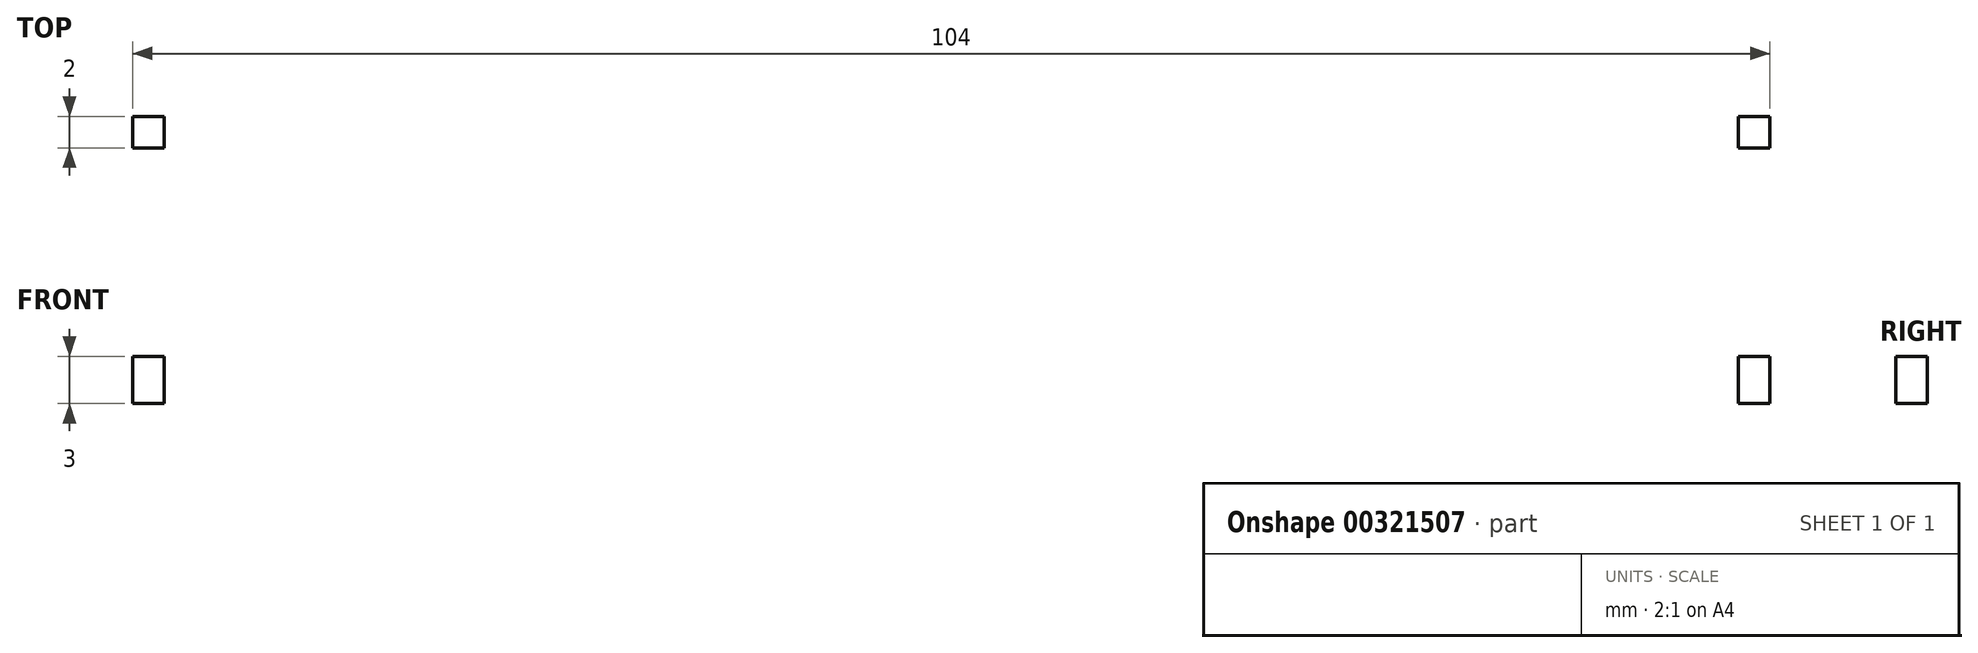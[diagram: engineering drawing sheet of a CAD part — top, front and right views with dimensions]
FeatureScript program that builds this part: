
annotation { "Feature Type Name" : "Feature", "Feature Type Description" : "" }
export const myFeature = defineFeature(function(context is Context, id is Id, definition is map)
    precondition{}
    {
        {
            var Q0;
            Q0=qCreatedBy(makeId("Top.planeOp"),FACE);
            var sketch = newSketch(context, id + "F0", { "sketchPlane" : qUnion([Q0])});
            skLineSegment(sketch, "E0.bottom", {"start": v(-52, 52) * mm, "end": v(52, 52) * mm});
            skLineSegment(sketch, "E0.top", {"start": v(-52, -52) * mm, "end": v(52, -52) * mm});
            skLineSegment(sketch, "E0.left", {"start": v(-52, 52) * mm, "end": v(-52, -52) * mm});
            skLineSegment(sketch, "E0.right", {"start": v(52, 52) * mm, "end": v(52, -52) * mm});
            skPoint(sketch, "E0.middle", {"position": v(0, 0) * mm});
            skLineSegment(sketch, "E1.bottom", {"start": v(-52, 52) * mm, "end": v(-50, 52) * mm});
            skLineSegment(sketch, "E1.top", {"start": v(-52, 50) * mm, "end": v(-50, 50) * mm});
            skLineSegment(sketch, "E1.left", {"start": v(-52, 52) * mm, "end": v(-52, 50) * mm});
            skLineSegment(sketch, "E1.right", {"start": v(-50, 52) * mm, "end": v(-50, 50) * mm});
            skLineSegment(sketch, "E2.bottom", {"start": v(-52, -52) * mm, "end": v(-50, -52) * mm});
            skLineSegment(sketch, "E2.top", {"start": v(-52, -50) * mm, "end": v(-50, -50) * mm});
            skLineSegment(sketch, "E2.left", {"start": v(-52, -52) * mm, "end": v(-52, -50) * mm});
            skLineSegment(sketch, "E2.right", {"start": v(-50, -52) * mm, "end": v(-50, -50) * mm});
            skLineSegment(sketch, "E3.bottom", {"start": v(52, -52) * mm, "end": v(50, -52) * mm});
            skLineSegment(sketch, "E3.top", {"start": v(52, -50) * mm, "end": v(50, -50) * mm});
            skLineSegment(sketch, "E3.left", {"start": v(52, -52) * mm, "end": v(52, -50) * mm});
            skLineSegment(sketch, "E3.right", {"start": v(50, -52) * mm, "end": v(50, -50) * mm});
            skLineSegment(sketch, "E4.bottom", {"start": v(52, 52) * mm, "end": v(50, 52) * mm});
            skLineSegment(sketch, "E4.top", {"start": v(52, 50) * mm, "end": v(50, 50) * mm});
            skLineSegment(sketch, "E4.left", {"start": v(52, 52) * mm, "end": v(52, 50) * mm});
            skLineSegment(sketch, "E4.right", {"start": v(50, 52) * mm, "end": v(50, 50) * mm});
            skSolve(sketch);
        }
        {
            var Q0;
            Q0=makeQuery(id+"F0.imprint","IMPRINT",FACE,{"disambiguationData":[TD([[makeQuery(id+"F0.imprint","IMPRINT",EDGE,{"derivedFrom":sQuery(id+"F0.wireOp",EDGE,"E0.bottom")}),-1.0]])]});
            extrude(context, id + "F1", {"entities" : qUnion([Q0]), "endBound" : BoundingType.SYMMETRIC, "depth" : 3 * mm});
        }
    });
